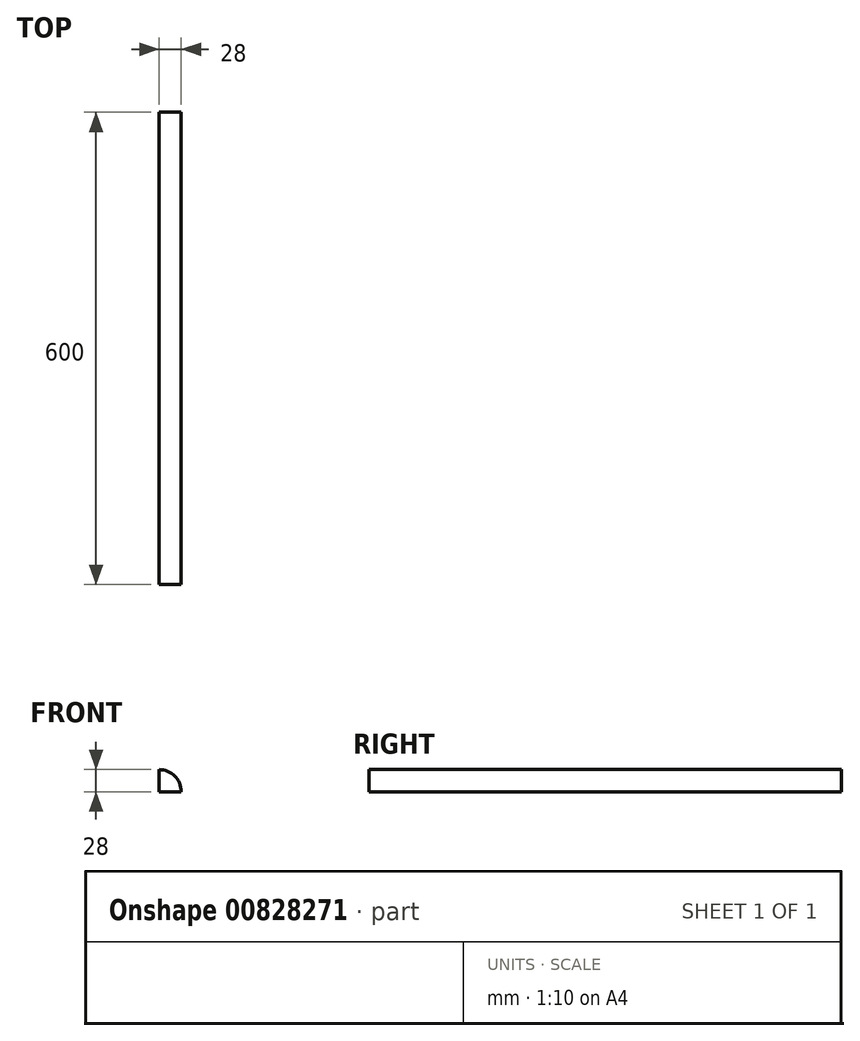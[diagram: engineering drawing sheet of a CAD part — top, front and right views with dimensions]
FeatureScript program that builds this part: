
annotation { "Feature Type Name" : "Feature", "Feature Type Description" : "" }
export const myFeature = defineFeature(function(context is Context, id is Id, definition is map)
    precondition{}
    {
        {
            var Q0;
            Q0=qCreatedBy(makeId("Front.planeOp"),FACE);
            var sketch = newSketch(context, id + "F0", { "sketchPlane" : qUnion([Q0])});
            skLineSegment(sketch, "E0", {"start": v(28, 0) * mm, "end": v(0, 0) * mm});
            skLineSegment(sketch, "E1", {"start": v(0, 0) * mm, "end": v(0, 28) * mm});
            skArc(sketch, "E2", {"start": v(28, 0) * mm, "mid": v(19.8, 19.8) * mm, "end": v(0, 28) * mm});
            skSolve(sketch);
        }
        {
            var Q0;
            Q0=makeQuery(id+"F0.imprint","IMPRINT",FACE,{"disambiguationData":[TD([[makeQuery(id+"F0.imprint","IMPRINT",EDGE,{"derivedFrom":sQuery(id+"F0.wireOp",EDGE,"E0")}),-1.0]])]});
            extrude(context, id + "F1", {"entities" : qUnion([Q0]), "endBound" : BoundingType.SYMMETRIC, "depth" : 600 * mm, "offsetDistance" : 25 * mm});
        }
    });
